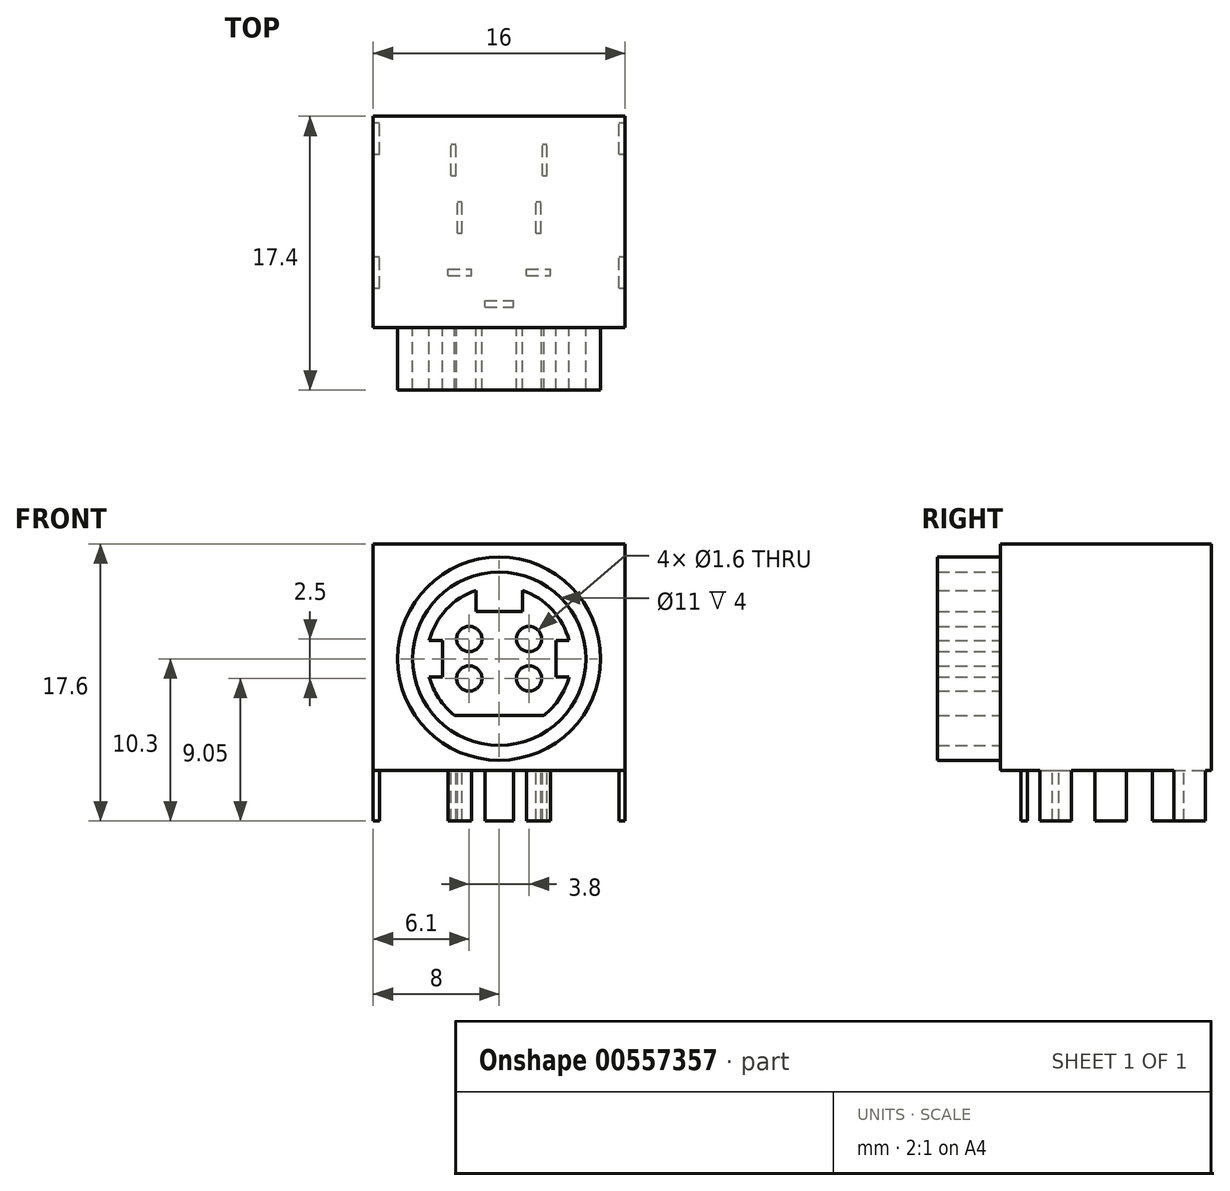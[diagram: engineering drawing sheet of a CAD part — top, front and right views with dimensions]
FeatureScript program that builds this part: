
annotation { "Feature Type Name" : "Feature", "Feature Type Description" : "" }
export const myFeature = defineFeature(function(context is Context, id is Id, definition is map)
    precondition{}
    {
        {
            var Q0;
            Q0=qCreatedBy(makeId("Top.planeOp"),FACE);
            var sketch = newSketch(context, id + "F0", { "sketchPlane" : qUnion([Q0])});
            skLineSegment(sketch, "E0.bottom", {"start": v(8, -6.7) * mm, "end": v(-8, -6.7) * mm});
            skLineSegment(sketch, "E0.top", {"start": v(8, 6.7) * mm, "end": v(-8, 6.7) * mm});
            skLineSegment(sketch, "E0.left", {"start": v(8, -6.7) * mm, "end": v(8, 6.7) * mm});
            skLineSegment(sketch, "E0.right", {"start": v(-8, -6.7) * mm, "end": v(-8, 6.7) * mm});
            skPoint(sketch, "E0.middle", {"position": v(0, 0) * mm});
            skSolve(sketch);
        }
        {
            var Q0;
            Q0 = qSketchRegion(id + "F0", true);
            extrude(context, id + "F1", {"entities" : qUnion([Q0]), "depth" : 14.4 * mm, "offsetDistance" : 25 * mm});
        }
        {
            var Q0;
            Q0=makeQuery(id+"F1.opExtrude","SWEPT_FACE",FACE,{"disambiguationData":[OSD([sQuery(id+"F0.wireOp",EDGE,"E0.bottom")])]});
            var sketch = newSketch(context, id + "F2", { "sketchPlane" : qUnion([Q0])});
            skCircle(sketch, "E1", {"center": v(0, 7.1) * mm, "radius": 6.45 * mm});
            skCircle(sketch, "E2", {"center": v(0, 7.1) * mm, "radius": 5.5 * mm});
            skSolve(sketch);
        }
        {
            var Q0;
            Q0 = qSketchRegion(id + "F2", true);
            extrude(context, id + "F3", {"entities" : qUnion([Q0]), "operationType" : NewBodyOperationType.ADD, "depth" : 4 * mm, "offsetDistance" : 25 * mm});
        }
        {
            var Q0;
            Q0=makeQuery(id+"F3.boolean.opBoolean","SPLIT",FACE,{"disambiguationData":[TD([makeQuery(id+"F3.opExtrude","SWEPT_FACE",FACE,{"disambiguationData":[OSD([sQuery(id+"F2.wireOp",EDGE,"E2")])]})])],"derivedFrom":makeQuery(id+"F1.opExtrude","SWEPT_FACE",FACE,{"disambiguationData":[OSD([sQuery(id+"F0.wireOp",EDGE,"E0.bottom")])]})});
            var sketch = newSketch(context, id + "F4", { "sketchPlane" : qUnion([Q0])});
            skArc(sketch, "E3", {"start": v(-4.44, 5.95) * mm, "mid": v(-3.84, 4.6) * mm, "end": v(-2.84, 3.5) * mm});
            skLineSegment(sketch, "E4", {"start": v(-1.48, 11.44) * mm, "end": v(-1.48, 10.1) * mm});
            skLineSegment(sketch, "E5", {"start": v(-1.48, 10.1) * mm, "end": v(1.47, 10.1) * mm});
            skLineSegment(sketch, "E6", {"start": v(1.47, 10.1) * mm, "end": v(1.47, 11.44) * mm});
            skLineSegment(sketch, "E7", {"start": v(4.44, 8.25) * mm, "end": v(3.6, 8.25) * mm});
            skLineSegment(sketch, "E8", {"start": v(3.6, 8.25) * mm, "end": v(3.6, 5.95) * mm});
            skLineSegment(sketch, "E9", {"start": v(3.6, 5.95) * mm, "end": v(4.44, 5.95) * mm});
            skLineSegment(sketch, "E10", {"start": v(-4.44, 8.25) * mm, "end": v(-3.6, 8.25) * mm});
            skLineSegment(sketch, "E11", {"start": v(-3.6, 8.25) * mm, "end": v(-3.6, 5.95) * mm});
            skLineSegment(sketch, "E12", {"start": v(-3.6, 5.95) * mm, "end": v(-4.44, 5.95) * mm});
            skLineSegment(sketch, "E13", {"start": v(-2.84, 3.5) * mm, "end": v(2.84, 3.5) * mm});
            skArc(sketch, "E14.trimOffspring", {"start": v(-1.48, 11.44) * mm, "mid": v(-3.36, 10.22) * mm, "end": v(-4.44, 8.25) * mm});
            skArc(sketch, "E15.trimOffspring", {"start": v(4.44, 8.25) * mm, "mid": v(3.36, 10.22) * mm, "end": v(1.48, 11.44) * mm});
            skArc(sketch, "E16.trimOffspring", {"start": v(2.84, 3.5) * mm, "mid": v(3.84, 4.6) * mm, "end": v(4.44, 5.95) * mm});
            skCircle(sketch, "E17", {"center": v(-1.9, 8.35) * mm, "radius": 0.8 * mm});
            skCircle(sketch, "E18", {"center": v(1.9, 8.35) * mm, "radius": 0.8 * mm});
            skCircle(sketch, "E19", {"center": v(-1.9, 5.85) * mm, "radius": 0.8 * mm});
            skCircle(sketch, "E20", {"center": v(1.9, 5.85) * mm, "radius": 0.8 * mm});
            skLineSegment(sketch, "E21", {"start": v(1.9, 8.35) * mm, "end": v(-1.9, 8.35) * mm, "construction": true});
            skLineSegment(sketch, "E22", {"start": v(-1.9, 8.35) * mm, "end": v(-1.9, 5.85) * mm, "construction": true});
            skLineSegment(sketch, "E23", {"start": v(-1.9, 5.85) * mm, "end": v(1.9, 5.85) * mm, "construction": true});
            skLineSegment(sketch, "E24", {"start": v(1.9, 5.85) * mm, "end": v(1.9, 8.35) * mm, "construction": true});
            skSolve(sketch);
        }
        {
            var Q0;
            Q0 = qSketchRegion(id + "F4", true);
            extrude(context, id + "F5", {"entities" : qUnion([Q0]), "depth" : 4 * mm, "offsetDistance" : 25 * mm});
        }
        {
            var Q0;
            Q0=makeQuery(id+"F1.opExtrude","CAP_FACE",FACE,{"disambiguationData":[OSD([sQuery(id+"F0.wireOp",EDGE,"E0.bottom"),sQuery(id+"F0.wireOp",EDGE,"E0.top"),sQuery(id+"F0.wireOp",EDGE,"E0.left"),sQuery(id+"F0.wireOp",EDGE,"E0.right")])],"isStart":true});
            var sketch = newSketch(context, id + "F6", { "sketchPlane" : qUnion([Q0])});
            skLineSegment(sketch, "E25.bottom", {"start": v(-0.9, 5.4) * mm, "end": v(0.9, 5.4) * mm});
            skLineSegment(sketch, "E25.top", {"start": v(-0.9, 5) * mm, "end": v(0.9, 5) * mm});
            skLineSegment(sketch, "E25.left", {"start": v(-0.9, 5.4) * mm, "end": v(-0.9, 5) * mm});
            skLineSegment(sketch, "E25.right", {"start": v(0.9, 5.4) * mm, "end": v(0.9, 5) * mm});
            skLineSegment(sketch, "E26.bottom", {"start": v(7.6, 4.2) * mm, "end": v(8, 4.2) * mm});
            skLineSegment(sketch, "E26.top", {"start": v(7.6, 2.2) * mm, "end": v(8, 2.2) * mm});
            skLineSegment(sketch, "E26.left", {"start": v(7.6, 4.2) * mm, "end": v(7.6, 2.2) * mm});
            skLineSegment(sketch, "E26.right", {"start": v(8, 4.2) * mm, "end": v(8, 2.2) * mm});
            skLineSegment(sketch, "E27.bottom", {"start": v(7.6, -4.3) * mm, "end": v(8, -4.3) * mm});
            skLineSegment(sketch, "E27.top", {"start": v(7.6, -6.3) * mm, "end": v(8, -6.3) * mm});
            skLineSegment(sketch, "E27.left", {"start": v(7.6, -4.3) * mm, "end": v(7.6, -6.3) * mm});
            skLineSegment(sketch, "E27.right", {"start": v(8, -4.3) * mm, "end": v(8, -6.3) * mm});
            skLineSegment(sketch, "E28.bottom", {"start": v(-8, 4.2) * mm, "end": v(-7.6, 4.2) * mm});
            skLineSegment(sketch, "E28.top", {"start": v(-8, 2.2) * mm, "end": v(-7.6, 2.2) * mm});
            skLineSegment(sketch, "E28.left", {"start": v(-8, 4.2) * mm, "end": v(-8, 2.2) * mm});
            skLineSegment(sketch, "E28.right", {"start": v(-7.6, 4.2) * mm, "end": v(-7.6, 2.2) * mm});
            skLineSegment(sketch, "E29.bottom", {"start": v(-8, -4.3) * mm, "end": v(-7.6, -4.3) * mm});
            skLineSegment(sketch, "E29.top", {"start": v(-8, -6.3) * mm, "end": v(-7.6, -6.3) * mm});
            skLineSegment(sketch, "E29.left", {"start": v(-8, -4.3) * mm, "end": v(-8, -6.3) * mm});
            skLineSegment(sketch, "E29.right", {"start": v(-7.6, -4.3) * mm, "end": v(-7.6, -6.3) * mm});
            skLineSegment(sketch, "E30", {"start": v(-7.7, 10.7) * mm, "end": v(7.68, 10.7) * mm, "construction": true});
            skLineSegment(sketch, "E31.bottom", {"start": v(-3.25, 3.4) * mm, "end": v(-1.75, 3.4) * mm});
            skLineSegment(sketch, "E31.top", {"start": v(-3.25, 3) * mm, "end": v(-1.75, 3) * mm});
            skLineSegment(sketch, "E31.left", {"start": v(-3.25, 3.4) * mm, "end": v(-3.25, 3) * mm});
            skLineSegment(sketch, "E31.right", {"start": v(-1.75, 3.4) * mm, "end": v(-1.75, 3) * mm});
            skLineSegment(sketch, "E32.bottom", {"start": v(1.75, 3.4) * mm, "end": v(3.25, 3.4) * mm});
            skLineSegment(sketch, "E32.top", {"start": v(1.75, 3) * mm, "end": v(3.25, 3) * mm});
            skLineSegment(sketch, "E32.left", {"start": v(1.75, 3.4) * mm, "end": v(1.75, 3) * mm});
            skLineSegment(sketch, "E32.right", {"start": v(3.25, 3.4) * mm, "end": v(3.25, 3) * mm});
            skSolve(sketch);
        }
        {
            var Q0;
            Q0 = qSketchRegion(id + "F6", true);
            extrude(context, id + "F7", {"entities" : qUnion([Q0]), "operationType" : NewBodyOperationType.ADD, "depth" : 3.2 * mm, "offsetDistance" : 25 * mm});
        }
        {
            var Q0;
            Q0=makeQuery(id+"F1.opExtrude","CAP_FACE",FACE,{"disambiguationData":[OSD([sQuery(id+"F0.wireOp",EDGE,"E0.bottom"),sQuery(id+"F0.wireOp",EDGE,"E0.top"),sQuery(id+"F0.wireOp",EDGE,"E0.left"),sQuery(id+"F0.wireOp",EDGE,"E0.right")])],"isStart":true});
            var sketch = newSketch(context, id + "F8", { "sketchPlane" : qUnion([Q0])});
            skLineSegment(sketch, "E33", {"start": v(-10.07, 10.7) * mm, "end": v(10.04, 10.7) * mm, "construction": true});
            skLineSegment(sketch, "E34.bottom", {"start": v(-2.65, 0.7) * mm, "end": v(-2.35, 0.7) * mm});
            skLineSegment(sketch, "E34.top", {"start": v(-2.65, -1.3) * mm, "end": v(-2.35, -1.3) * mm});
            skLineSegment(sketch, "E34.left", {"start": v(-2.65, 0.7) * mm, "end": v(-2.65, -1.3) * mm});
            skLineSegment(sketch, "E34.right", {"start": v(-2.35, 0.7) * mm, "end": v(-2.35, -1.3) * mm});
            skLineSegment(sketch, "E35.bottom", {"start": v(2.35, 0.7) * mm, "end": v(2.65, 0.7) * mm});
            skLineSegment(sketch, "E35.top", {"start": v(2.35, -1.3) * mm, "end": v(2.65, -1.3) * mm});
            skLineSegment(sketch, "E35.left", {"start": v(2.35, 0.7) * mm, "end": v(2.35, -1.3) * mm});
            skLineSegment(sketch, "E35.right", {"start": v(2.65, 0.7) * mm, "end": v(2.65, -1.3) * mm});
            skLineSegment(sketch, "E36.bottom", {"start": v(-3.05, -2.95) * mm, "end": v(-2.75, -2.95) * mm});
            skLineSegment(sketch, "E36.top", {"start": v(-3.05, -4.95) * mm, "end": v(-2.75, -4.95) * mm});
            skLineSegment(sketch, "E36.left", {"start": v(-3.05, -2.95) * mm, "end": v(-3.05, -4.95) * mm});
            skLineSegment(sketch, "E36.right", {"start": v(-2.75, -2.95) * mm, "end": v(-2.75, -4.95) * mm});
            skLineSegment(sketch, "E37.bottom", {"start": v(2.75, -2.95) * mm, "end": v(3.05, -2.95) * mm});
            skLineSegment(sketch, "E37.top", {"start": v(2.75, -4.95) * mm, "end": v(3.05, -4.95) * mm});
            skLineSegment(sketch, "E37.left", {"start": v(2.75, -2.95) * mm, "end": v(2.75, -4.95) * mm});
            skLineSegment(sketch, "E37.right", {"start": v(3.05, -2.95) * mm, "end": v(3.05, -4.95) * mm});
            skSolve(sketch);
        }
        {
            var Q0;
            Q0 = qSketchRegion(id + "F8", true);
            extrude(context, id + "F9", {"entities" : qUnion([Q0]), "depth" : 3.2 * mm, "offsetDistance" : 25 * mm});
        }
    });
